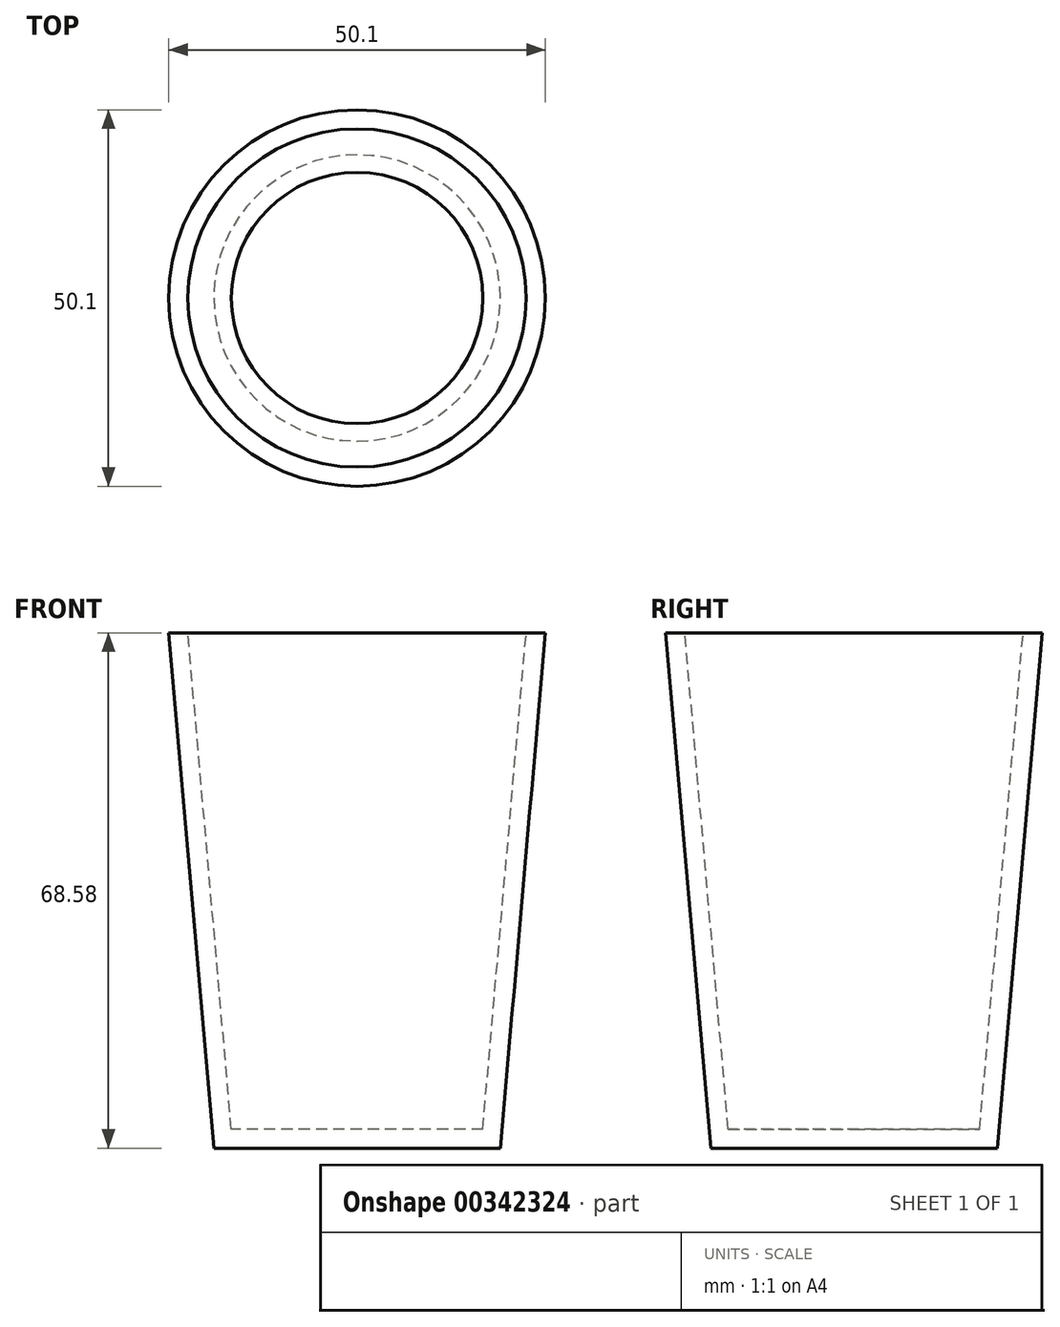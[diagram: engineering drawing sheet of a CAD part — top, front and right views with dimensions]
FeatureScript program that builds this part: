
annotation { "Feature Type Name" : "Feature", "Feature Type Description" : "" }
export const myFeature = defineFeature(function(context is Context, id is Id, definition is map)
    precondition{}
    {
        {
            var Q0;
            Q0=qCreatedBy(makeId("Top.planeOp"),FACE);
            var sketch = newSketch(context, id + "F0", { "sketchPlane" : qUnion([Q0])});
            skCircle(sketch, "E0", {"center": v(0, 0) * mm, "radius": 19.05 * mm});
            skSolve(sketch);
        }
        {
            var Q0;
            Q0=makeQuery(id+"F0.imprint","IMPRINT",FACE,{"disambiguationData":[TD([[makeQuery(id+"F0.imprint","IMPRINT",EDGE,{"derivedFrom":sQuery(id+"F0.wireOp",EDGE,"E0")}),1.0]])]});
            extrude(context, id + "F1", {"entities" : qUnion([Q0]), "depth" : 68.58 * mm, "hasDraft" : true, "draftAngle" : 5 * degree});
        }
        {
            var Q0;
            Q0=makeQuery(id+"F1.opExtrude","CAP_FACE",FACE,{"disambiguationData":[OSD([sQuery(id+"F0.wireOp",EDGE,"E0")])],"isStart":false});
            shell(context, id + "F2", {"entities" : qUnion([Q0]), "thickness" : 2.54 * mm});
        }
        {
            var Q0;
            Q0=qCreatedBy(makeId("Front.planeOp"),FACE);
            cPlane(context, id + "F3", {"entities" : qUnion([Q0]), "cplaneType" : CPlaneType.OFFSET, "offset" : 18.8 * mm, "width" : 152.4 * mm, "height" : 152.4 * mm});
        }
    });
